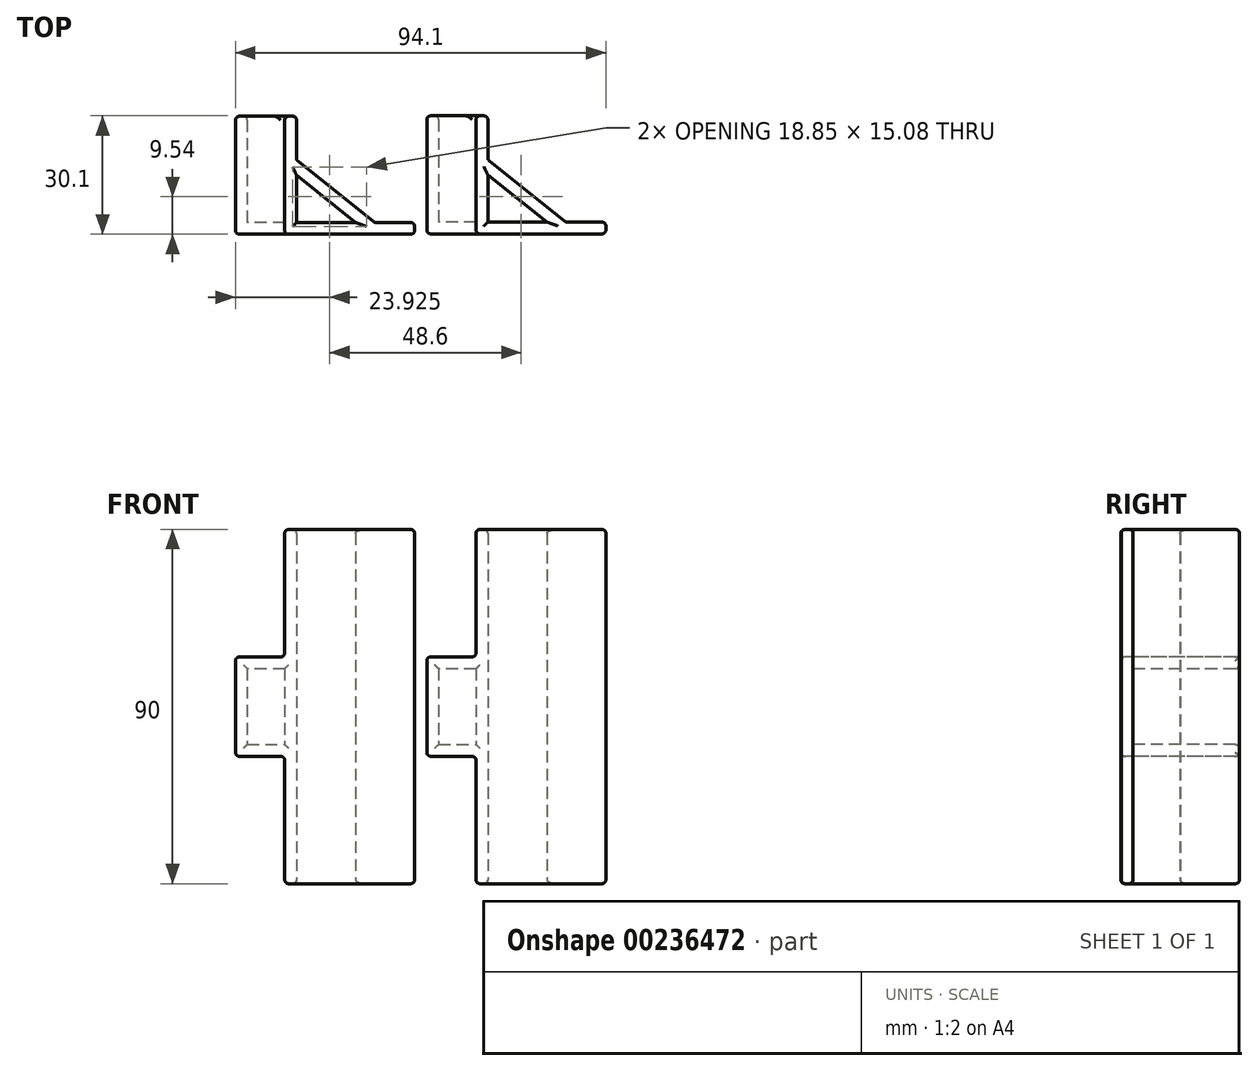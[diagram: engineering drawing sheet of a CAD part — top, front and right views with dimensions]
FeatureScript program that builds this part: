
annotation { "Feature Type Name" : "Feature", "Feature Type Description" : "" }
export const myFeature = defineFeature(function(context is Context, id is Id, definition is map)
    precondition{}
    {
        {
            var Q0;
            Q0=qCreatedBy(makeId("Top.planeOp"),FACE);
            var sketch = newSketch(context, id + "F0", { "sketchPlane" : qUnion([Q0])});
            skLineSegment(sketch, "E0.bottom", {"start": v(-1.5, 15) * mm, "end": v(1.5, 15) * mm});
            skLineSegment(sketch, "E0.top", {"start": v(-1.5, -15) * mm, "end": v(1.5, -15) * mm});
            skLineSegment(sketch, "E0.left", {"start": v(-1.5, 15) * mm, "end": v(-1.5, -15) * mm});
            skLineSegment(sketch, "E0.right", {"start": v(1.5, 15) * mm, "end": v(1.5, -15) * mm});
            skPoint(sketch, "E0.middle", {"position": v(0, 0) * mm});
            skLineSegment(sketch, "E1.bottom", {"start": v(1.5, -15) * mm, "end": v(31.5, -15) * mm});
            skLineSegment(sketch, "E1.top", {"start": v(1.5, -12) * mm, "end": v(31.5, -12) * mm});
            skLineSegment(sketch, "E1.left", {"start": v(1.5, -15) * mm, "end": v(1.5, -12) * mm});
            skLineSegment(sketch, "E1.right", {"start": v(31.5, -15) * mm, "end": v(31.5, -12) * mm});
            skPoint(sketch, "E2", {"position": v(1.5, 0) * mm});
            skPoint(sketch, "E3", {"position": v(16.5, -12) * mm});
            skLineSegment(sketch, "E4", {"start": v(1.5, 0) * mm, "end": v(16.5, -12) * mm});
            skPoint(sketch, "E5", {"position": v(9, -6) * mm});
            skLineSegment(sketch, "E6", {"start": v(1.5, 3.84) * mm, "end": v(21.3, -12) * mm});
            skSolve(sketch);
        }
        {
            var Q0;
            {var subQ1=sQuery(id+"F0.wireOp",EDGE,"E0.bottom");Q0=makeQuery(id+"F0.imprint","IMPRINT",FACE,{"disambiguationData":[TD([[makeQuery(id+"F0.imprint","IMPRINT",EDGE,{"derivedFrom":subQ1}),-1.0]])]});}
            var Q1;
            {var subQ0=sQuery(id+"F0.wireOp",EDGE,"E4");Q1=makeQuery(id+"F0.imprint","IMPRINT",FACE,{"disambiguationData":[TD([[makeQuery(id+"F0.imprint","IMPRINT",EDGE,{"derivedFrom":subQ0}),1.0]])]});}
            var Q2;
            Q2=makeQuery(id+"F0.imprint","IMPRINT",FACE,{"disambiguationData":[TD([[makeQuery(id+"F0.imprint","IMPRINT",EDGE,{"derivedFrom":sQuery(id+"F0.wireOp",EDGE,"E1.bottom")}),1.0]])]});
            extrude(context, id + "F1", {"entities" : qUnion([Q0, Q1, Q2]), "depth" : 90 * mm, "offsetDistance" : 25 * mm});
        }
        {
            var Q0;
            Q0=makeQuery(id+"F1.opExtrude","SWEPT_FACE",FACE,{"disambiguationData":[OSD([sQuery(id+"F0.wireOp",EDGE,"E0.top"),sQuery(id+"F0.wireOp",EDGE,"E1.bottom")])]});
            var sketch = newSketch(context, id + "F2", { "sketchPlane" : qUnion([Q0])});
            skPoint(sketch, "E7", {"position": v(-1.5, 45) * mm});
            skPoint(sketch, "E8", {"position": v(-1.5, 54.63) * mm});
            skPoint(sketch, "E9", {"position": v(-1.5, 35.38) * mm});
            skPoint(sketch, "E10", {"position": v(-11, 54.63) * mm});
            skPoint(sketch, "E11", {"position": v(-11, 35.38) * mm});
            skLineSegment(sketch, "E12", {"start": v(-1.5, 54.63) * mm, "end": v(-11, 54.63) * mm});
            skLineSegment(sketch, "E13", {"start": v(-11, 54.63) * mm, "end": v(-11, 35.38) * mm});
            skLineSegment(sketch, "E14", {"start": v(-11, 35.38) * mm, "end": v(-1.5, 35.38) * mm});
            skLineSegment(sketch, "E15.0", {"start": v(-14, 32.38) * mm, "end": v(-1.5, 32.38) * mm});
            skLineSegment(sketch, "E15.1", {"start": v(-14, 57.62) * mm, "end": v(-14, 32.38) * mm});
            skLineSegment(sketch, "E15.2", {"start": v(-1.5, 57.62) * mm, "end": v(-14, 57.62) * mm});
            skSolve(sketch);
        }
        {
            var Q0;
            {var subQ0=sQuery(id+"F2.wireOp",EDGE,"E12");Q0=makeQuery(id+"F2.imprint","IMPRINT",FACE,{"disambiguationData":[TD([[makeQuery(id+"F2.imprint","IMPRINT",EDGE,{"derivedFrom":subQ0}),1.0]])]});}
            extrude(context, id + "F3", {"entities" : qUnion([Q0]), "oppositeDirection" : true, "depth" : 3 * mm, "offsetDistance" : 25 * mm});
        }
        {
            var Q0;
            {var subQ3=sQuery(id+"F2.wireOp",EDGE,"E12");Q0=makeQuery(id+"F2.imprint","IMPRINT",FACE,{"disambiguationData":[TD([[makeQuery(id+"F2.imprint","IMPRINT",EDGE,{"derivedFrom":subQ3}),-1.0]])]});}
            extrude(context, id + "F4", {"entities" : qUnion([Q0]), "oppositeDirection" : true, "depth" : 30 * mm, "offsetDistance" : 25 * mm});
        }
        {
            var Q0;
            Q0=makeQuery(id+"F1.opExtrude","SWEPT_BODY",BODY,{"disambiguationData":[OSD([sQuery(id+"F0.wireOp",EDGE,"E0.bottom"),sQuery(id+"F0.wireOp",EDGE,"E0.top"),sQuery(id+"F0.wireOp",EDGE,"E0.left"),sQuery(id+"F0.wireOp",EDGE,"E0.right"),sQuery(id+"F0.wireOp",EDGE,"E1.bottom"),sQuery(id+"F0.wireOp",EDGE,"E1.top"),sQuery(id+"F0.wireOp",EDGE,"E1.right"),sQuery(id+"F0.wireOp",EDGE,"E4"),sQuery(id+"F0.wireOp",EDGE,"E6")])]});
            var Q1;
            Q1=makeQuery(id+"F4.opExtrude","SWEPT_BODY",BODY,{"disambiguationData":[OSD([sQuery(id+"F0.wireOp",EDGE,"E0.top"),sQuery(id+"F0.wireOp",EDGE,"E0.left"),sQuery(id+"F2.wireOp",EDGE,"E12"),sQuery(id+"F2.wireOp",EDGE,"E13"),sQuery(id+"F2.wireOp",EDGE,"E14"),sQuery(id+"F2.wireOp",EDGE,"E15.0"),sQuery(id+"F2.wireOp",EDGE,"E15.1"),sQuery(id+"F2.wireOp",EDGE,"E15.2")])]});
            var Q2;
            Q2=makeQuery(id+"F3.opExtrude","SWEPT_BODY",BODY,{"disambiguationData":[OSD([sQuery(id+"F0.wireOp",EDGE,"E0.top"),sQuery(id+"F0.wireOp",EDGE,"E0.left"),sQuery(id+"F2.wireOp",EDGE,"E12"),sQuery(id+"F2.wireOp",EDGE,"E13"),sQuery(id+"F2.wireOp",EDGE,"E14")])]});
            booleanBodies(context, id + "F5", {"operationType" : BooleanOperationType.UNION, "tools" : qUnion([Q0, Q1, Q2])});
        }
        {
            var Q0;
            {var subQ0=sQuery(id+"F0.wireOp",EDGE,"E1.top");Q0=makeQuery(id+"F1.opExtrude","SWEPT_FACE",FACE,{"disambiguationData":[OSD([subQ0]),TDD([makeQuery(id+"F0.imprint","IMPRINT",EDGE,{"disambiguationData":[TD([[makeQuery(id+"F0.imprint","INTERSECT",VERTEX,{"derivedFrom":[subQ0,sQuery(id+"F0.wireOp",EDGE,"E1.right")]}),1.0]])],"derivedFrom":subQ0})])]});}
            var Q1;
            Q1=makeQuery(id+"F1.opExtrude","SWEPT_FACE",FACE,{"disambiguationData":[OSD([sQuery(id+"F0.wireOp",EDGE,"E6")])]});
            var Q2;
            {var subQ0=sQuery(id+"F0.wireOp",EDGE,"E0.right");Q2=makeQuery(id+"F1.opExtrude","SWEPT_FACE",FACE,{"disambiguationData":[OSD([subQ0]),TDD([makeQuery(id+"F0.imprint","IMPRINT",EDGE,{"disambiguationData":[TD([[makeQuery(id+"F0.imprint","INTERSECT",VERTEX,{"derivedFrom":[sQuery(id+"F0.wireOp",EDGE,"E0.bottom"),subQ0]}),-1.0]])],"derivedFrom":subQ0})])]});}
            var Q3;
            {var subQ2=sQuery(id+"F0.wireOp",EDGE,"E0.left");var subQ7=sQuery(id+"F2.wireOp",EDGE,"E15.2");Q3=makeQuery(id+"F5.opBoolean","SPLIT",FACE,{"disambiguationData":[TD([makeQuery(id+"F4.opExtrude","SWEPT_FACE",FACE,{"disambiguationData":[OSD([subQ7])]})])],"derivedFrom":makeQuery(id+"F1.opExtrude","SWEPT_FACE",FACE,{"disambiguationData":[OSD([subQ2])]})});}
            var Q4;
            Q4=makeQuery(id+"F4.opExtrude","SWEPT_FACE",FACE,{"disambiguationData":[OSD([sQuery(id+"F2.wireOp",EDGE,"E15.1")])]});
            var Q5;
            {var subQ2=sQuery(id+"F2.wireOp",EDGE,"E15.0");var subQ3=sQuery(id+"F0.wireOp",EDGE,"E0.left");Q5=makeQuery(id+"F5.opBoolean","SPLIT",FACE,{"disambiguationData":[TD([makeQuery(id+"F4.opExtrude","SWEPT_FACE",FACE,{"disambiguationData":[OSD([subQ2])]})])],"derivedFrom":makeQuery(id+"F1.opExtrude","SWEPT_FACE",FACE,{"disambiguationData":[OSD([subQ3])]})});}
            var Q6;
            {var subQ0=sQuery(id+"F2.wireOp",EDGE,"E14");var subQ1=sQuery(id+"F2.wireOp",EDGE,"E13");var subQ2=sQuery(id+"F2.wireOp",EDGE,"E12");var subQ3=sQuery(id+"F0.wireOp",EDGE,"E0.left");var subQ4=sQuery(id+"F0.wireOp",EDGE,"E0.top");Q6=makeQuery(id+"F5.opBoolean","MERGE",FACE,{"derivedFrom":[makeQuery(id+"F1.opExtrude","SWEPT_FACE",FACE,{"disambiguationData":[OSD([subQ4,sQuery(id+"F0.wireOp",EDGE,"E1.bottom")])]}),makeQuery(id+"F3.opExtrude","CAP_FACE",FACE,{"disambiguationData":[OSD([subQ4,subQ3,subQ2,subQ1,subQ0])],"isStart":true}),makeQuery(id+"F4.opExtrude","CAP_FACE",FACE,{"disambiguationData":[OSD([subQ4,subQ3,subQ2,subQ1,subQ0,sQuery(id+"F2.wireOp",EDGE,"E15.0"),sQuery(id+"F2.wireOp",EDGE,"E15.1"),sQuery(id+"F2.wireOp",EDGE,"E15.2")])],"isStart":true})]});}
            var Q7;
            {var subQ0=sQuery(id+"F0.wireOp",EDGE,"E0.right");Q7=makeQuery(id+"F1.opExtrude","CAP_EDGE",EDGE,{"disambiguationData":[OSD([subQ0]),TDD([makeQuery(id+"F0.imprint","IMPRINT",EDGE,{"disambiguationData":[TD([[makeQuery(id+"F0.imprint","INTERSECT",VERTEX,{"derivedFrom":[subQ0,sQuery(id+"F0.wireOp",EDGE,"E4")]}),-1.0]])],"derivedFrom":subQ0})])],"isStart":true});}
            var Q8;
            Q8=makeQuery(id+"F1.opExtrude","CAP_EDGE",EDGE,{"disambiguationData":[OSD([sQuery(id+"F0.wireOp",EDGE,"E4")])],"isStart":true});
            var Q9;
            {var subQ0=sQuery(id+"F0.wireOp",EDGE,"E1.top");Q9=makeQuery(id+"F1.opExtrude","CAP_EDGE",EDGE,{"disambiguationData":[OSD([subQ0]),TDD([makeQuery(id+"F0.imprint","IMPRINT",EDGE,{"disambiguationData":[TD([[makeQuery(id+"F0.imprint","INTERSECT",VERTEX,{"derivedFrom":[subQ0,sQuery(id+"F0.wireOp",EDGE,"E4")]}),1.0]])],"derivedFrom":subQ0})])],"isStart":true});}
            var Q10;
            {var subQ0=sQuery(id+"F0.wireOp",EDGE,"E0.right");Q10=makeQuery(id+"F1.opExtrude","CAP_EDGE",EDGE,{"disambiguationData":[OSD([subQ0]),TDD([makeQuery(id+"F0.imprint","IMPRINT",EDGE,{"disambiguationData":[TD([[makeQuery(id+"F0.imprint","INTERSECT",VERTEX,{"derivedFrom":[subQ0,sQuery(id+"F0.wireOp",EDGE,"E4")]}),-1.0]])],"derivedFrom":subQ0})])],"isStart":false});}
            var Q11;
            Q11=makeQuery(id+"F1.opExtrude","CAP_EDGE",EDGE,{"disambiguationData":[OSD([sQuery(id+"F0.wireOp",EDGE,"E4")])],"isStart":false});
            var Q12;
            {var subQ0=sQuery(id+"F0.wireOp",EDGE,"E1.top");Q12=makeQuery(id+"F1.opExtrude","CAP_EDGE",EDGE,{"disambiguationData":[OSD([subQ0]),TDD([makeQuery(id+"F0.imprint","IMPRINT",EDGE,{"disambiguationData":[TD([[makeQuery(id+"F0.imprint","INTERSECT",VERTEX,{"derivedFrom":[subQ0,sQuery(id+"F0.wireOp",EDGE,"E4")]}),1.0]])],"derivedFrom":subQ0})])],"isStart":false});}
            var Q13;
            Q13=makeQuery(id+"F1.opExtrude","CAP_EDGE",EDGE,{"disambiguationData":[OSD([sQuery(id+"F0.wireOp",EDGE,"E0.bottom")])],"isStart":false});
            var Q14;
            Q14=makeQuery(id+"F1.opExtrude","CAP_EDGE",EDGE,{"disambiguationData":[OSD([sQuery(id+"F0.wireOp",EDGE,"E1.right")])],"isStart":false});
            var Q15;
            Q15=makeQuery(id+"F1.opExtrude","CAP_EDGE",EDGE,{"disambiguationData":[OSD([sQuery(id+"F0.wireOp",EDGE,"E0.bottom")])],"isStart":true});
            var Q16;
            Q16=makeQuery(id+"F1.opExtrude","CAP_FACE",FACE,{"disambiguationData":[OSD([sQuery(id+"F0.wireOp",EDGE,"E0.bottom"),sQuery(id+"F0.wireOp",EDGE,"E0.top"),sQuery(id+"F0.wireOp",EDGE,"E0.left"),sQuery(id+"F0.wireOp",EDGE,"E0.right"),sQuery(id+"F0.wireOp",EDGE,"E1.bottom"),sQuery(id+"F0.wireOp",EDGE,"E1.top"),sQuery(id+"F0.wireOp",EDGE,"E1.right"),sQuery(id+"F0.wireOp",EDGE,"E4"),sQuery(id+"F0.wireOp",EDGE,"E6")])],"isStart":true});
            var Q17;
            Q17=makeQuery(id+"F4.opExtrude","CAP_EDGE",EDGE,{"disambiguationData":[OSD([sQuery(id+"F2.wireOp",EDGE,"E13")])],"isStart":false});
            var Q18;
            Q18=makeQuery(id+"F4.opExtrude","CAP_EDGE",EDGE,{"disambiguationData":[OSD([sQuery(id+"F2.wireOp",EDGE,"E14")])],"isStart":false});
            var Q19;
            {var subQ1=sQuery(id+"F2.wireOp",EDGE,"E12");var subQ2=sQuery(id+"F0.wireOp",EDGE,"E0.left");var subQ3=sQuery(id+"F0.wireOp",EDGE,"E0.bottom");Q19=makeQuery(id+"F5.opBoolean","SPLIT",EDGE,{"disambiguationData":[TD([makeQuery(id+"F4.opExtrude","SWEPT_FACE",FACE,{"disambiguationData":[OSD([subQ1])]})])],"derivedFrom":makeQuery(id+"F1.opExtrude","SWEPT_EDGE",EDGE,{"disambiguationData":[OSD([subQ3,subQ2])]})});}
            var Q20;
            Q20=makeQuery(id+"F4.opExtrude","CAP_EDGE",EDGE,{"disambiguationData":[OSD([sQuery(id+"F2.wireOp",EDGE,"E12")])],"isStart":false});
            fillet(context, id + "F6", {"entities" : qUnion([Q0, Q1, Q2, Q3, Q4, Q5, Q6, Q7, Q8, Q9, Q10, Q11, Q12, Q13, Q14, Q15, Q16, Q17, Q18, Q19, Q20]), "tangentPropagation" : true, "radius" : 1 * mm, "defaultsChanged" : false, "vertexSettings" : [], "allowEdgeOverflow" : false});
        }
        {
            var Q0;
            Q0=makeQuery(id+"F1.opExtrude","SWEPT_BODY",BODY,{"disambiguationData":[OSD([sQuery(id+"F0.wireOp",EDGE,"E0.bottom"),sQuery(id+"F0.wireOp",EDGE,"E0.top"),sQuery(id+"F0.wireOp",EDGE,"E0.left"),sQuery(id+"F0.wireOp",EDGE,"E0.right"),sQuery(id+"F0.wireOp",EDGE,"E1.bottom"),sQuery(id+"F0.wireOp",EDGE,"E1.top"),sQuery(id+"F0.wireOp",EDGE,"E1.right"),sQuery(id+"F0.wireOp",EDGE,"E4"),sQuery(id+"F0.wireOp",EDGE,"E6")])]});
            transform(context, id + "F7", {"entities" : qUnion([Q0]), "transformType" : TransformType.TRANSLATION_3D, "dx" : -48.6 * mm, "dy" : -0.1 * mm, "dz" : 0 * mm, "makeCopy" : true});
        }
    });
